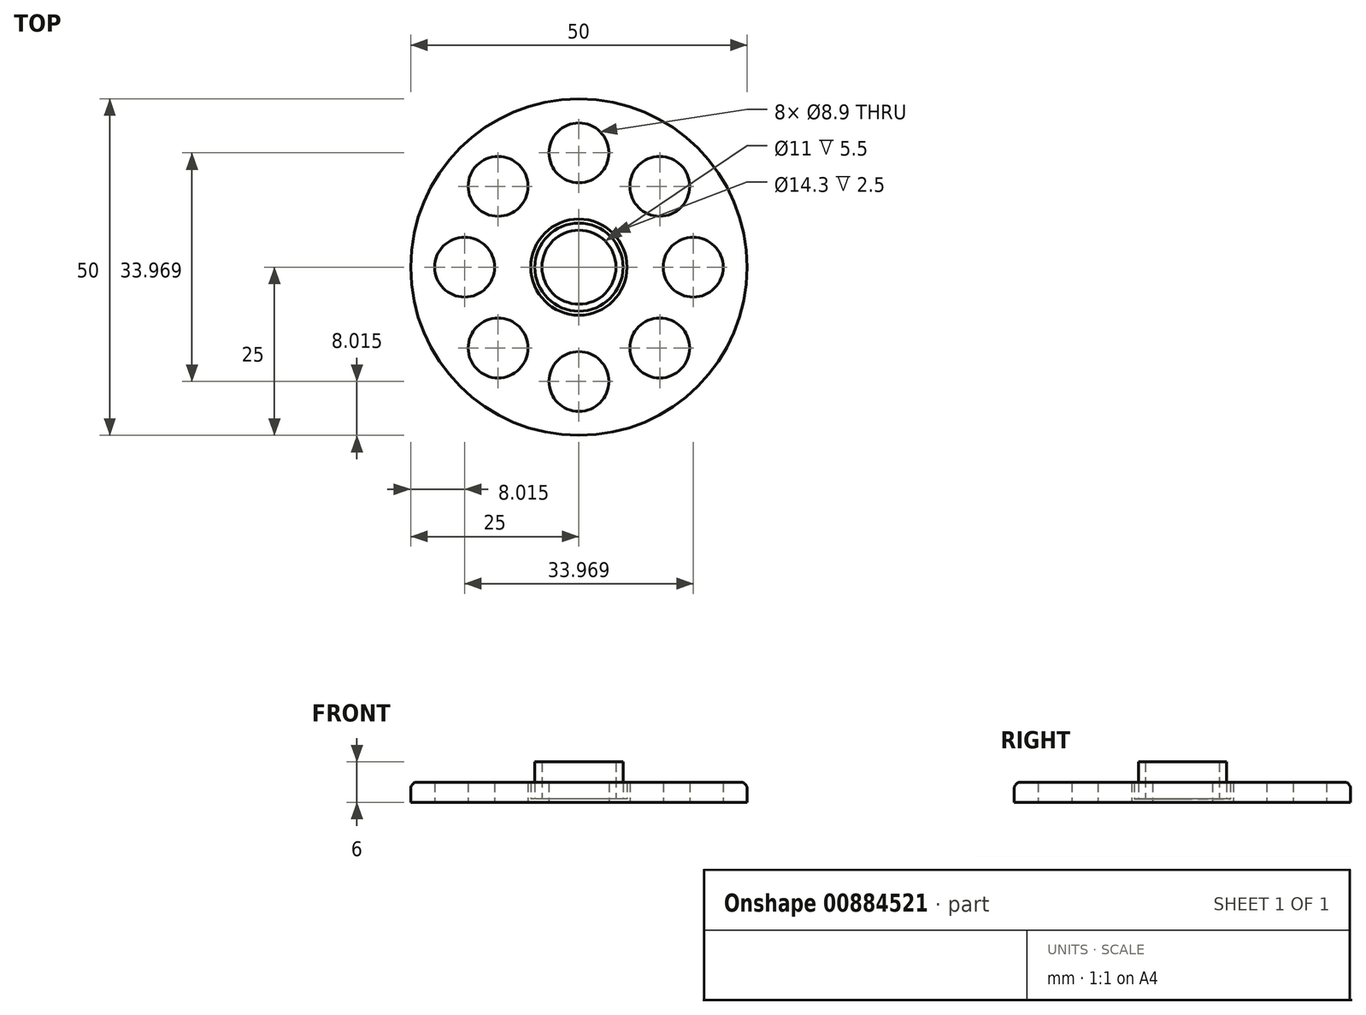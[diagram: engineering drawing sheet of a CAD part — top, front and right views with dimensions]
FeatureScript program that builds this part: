
annotation { "Feature Type Name" : "Feature", "Feature Type Description" : "" }
export const myFeature = defineFeature(function(context is Context, id is Id, definition is map)
    precondition{}
    {
        {
            var Q0;
            Q0=qCreatedBy(makeId("Top.planeOp"),FACE);
            var sketch = newSketch(context, id + "F0", { "sketchPlane" : qUnion([Q0])});
            skCircle(sketch, "E0", {"center": v(0, 0) * mm, "radius": 6.55 * mm});
            skCircle(sketch, "E1", {"center": v(0, 0) * mm, "radius": 7.15 * mm});
            skCircle(sketch, "E2", {"center": v(0, 0) * mm, "radius": 5.5 * mm});
            skCircle(sketch, "E3", {"center": v(0, 0) * mm, "radius": 25 * mm});
            skCircle(sketch, "E4", {"center": v(0, 16.98) * mm, "radius": 4.45 * mm});
            skCircle(sketch, "E5.1.0", {"center": v(-12, 12) * mm, "radius": 4.45 * mm});
            skCircle(sketch, "E5.2.0", {"center": v(-16.98, 0) * mm, "radius": 4.45 * mm});
            skCircle(sketch, "E5.3.0", {"center": v(-12, -12) * mm, "radius": 4.45 * mm});
            skCircle(sketch, "E5.4.0", {"center": v(0, -16.98) * mm, "radius": 4.45 * mm});
            skCircle(sketch, "E5.5.0", {"center": v(12, -12) * mm, "radius": 4.45 * mm});
            skCircle(sketch, "E5.6.0", {"center": v(16.98, 0) * mm, "radius": 4.45 * mm});
            skCircle(sketch, "E5.7.0", {"center": v(12, 12) * mm, "radius": 4.45 * mm});
            skSolve(sketch);
        }
        {
            var Q0;
            Q0=makeQuery(id+"F0.imprint","IMPRINT",FACE,{"disambiguationData":[TD([[makeQuery(id+"F0.imprint","IMPRINT",EDGE,{"derivedFrom":sQuery(id+"F0.wireOp",EDGE,"E0")}),1.0]])]});
            extrude(context, id + "F1", {"entities" : qUnion([Q0]), "depth" : 6 * mm, "offsetDistance" : 25 * mm});
        }
        {
            var Q0;
            Q0=makeQuery(id+"F0.imprint","IMPRINT",FACE,{"disambiguationData":[TD([[makeQuery(id+"F0.imprint","IMPRINT",EDGE,{"derivedFrom":sQuery(id+"F0.wireOp",EDGE,"E0")}),-1.0]])]});
            var Q1;
            Q1=makeQuery(id+"F0.imprint","IMPRINT",FACE,{"disambiguationData":[TD([[makeQuery(id+"F0.imprint","IMPRINT",EDGE,{"derivedFrom":sQuery(id+"F0.wireOp",EDGE,"E2")}),1.0]])]});
            extrude(context, id + "F2", {"entities" : qUnion([Q0, Q1]), "operationType" : NewBodyOperationType.ADD, "depth" : .5 * mm, "offsetDistance" : 25 * mm});
        }
        {
            var Q0;
            Q0=makeQuery(id+"F0.imprint","IMPRINT",FACE,{"disambiguationData":[TD([[makeQuery(id+"F0.imprint","IMPRINT",EDGE,{"derivedFrom":sQuery(id+"F0.wireOp",EDGE,"E1")}),-1.0]])]});
            extrude(context, id + "F3", {"entities" : qUnion([Q0]), "operationType" : NewBodyOperationType.ADD, "depth" : 3 * mm, "offsetDistance" : 25 * mm});
        }
        {
            var Q0;
            Q0=makeQuery(id+"F3.opExtrude","CAP_EDGE",EDGE,{"disambiguationData":[OSD([sQuery(id+"F0.wireOp",EDGE,"E3")])],"isStart":false});
            fillet(context, id + "F4", {"entities" : qUnion([Q0]), "radius" : 1 * mm, "tangentPropagation" : true, "allowEdgeOverflow" : false});
        }
    });
